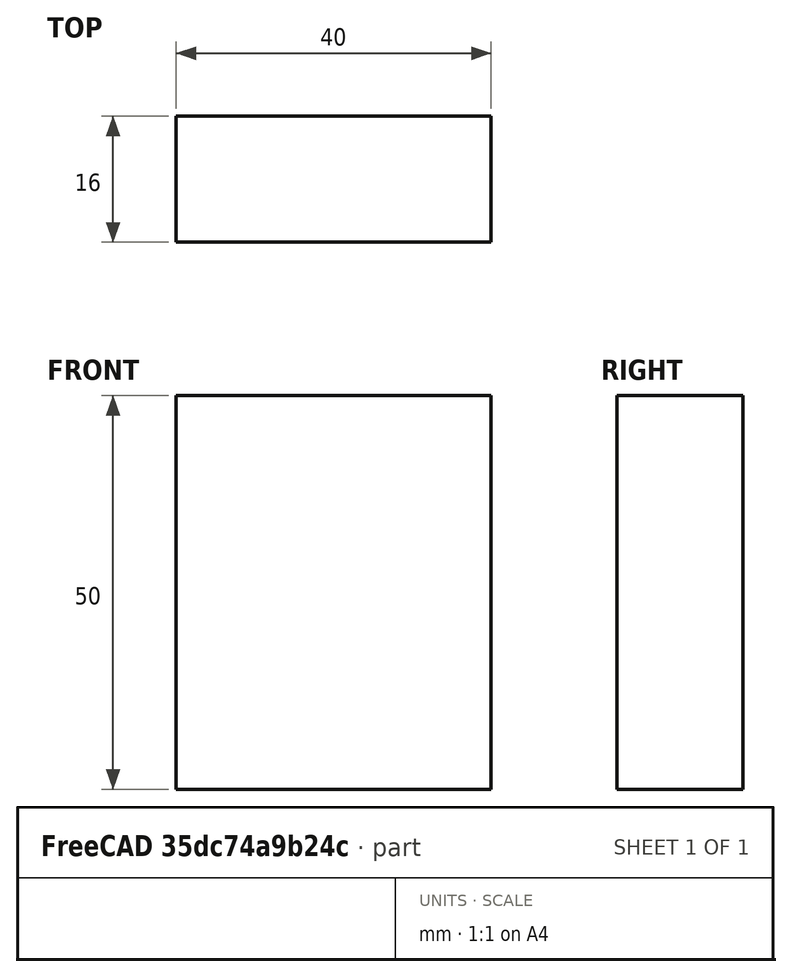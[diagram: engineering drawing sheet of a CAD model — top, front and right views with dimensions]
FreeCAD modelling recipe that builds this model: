
FCSTD DOCUMENT  (FreeCAD 0.15R4671 (Git))
Label: Flat Bar 40x16 EN10058 S235JR
License: All rights reserved
LicenseURL: http://en.wikipedia.org/wiki/All_rights_reserved
objects: Sketcher::SketchObject×1, Part::Extrusion×1
note: 2 computed .brp shape members not serialized (recipe doc carries the construction recipe); baked Part::Feature solids carry a one-line shape summary decoded from their .brp

FEATURE [Sketcher::SketchObject] Sketch
  sketch-geometry (4):
    g0: LineSegment StartX=-20 StartY=-8 StartZ=0 EndX=20 EndY=-8 EndZ=0
    g1: LineSegment StartX=20 StartY=-8 StartZ=0 EndX=20 EndY=8 EndZ=0
    g2: LineSegment StartX=20 StartY=8 StartZ=0 EndX=-20 EndY=8 EndZ=0
    g3: LineSegment StartX=-20 StartY=8 StartZ=0 EndX=-20 EndY=-8 EndZ=0
  constraints (12):
    c: Coincident(g0,g1)
    c: Coincident(g1,g2)
    c: Coincident(g2,g3)
    c: Coincident(g3,g0)
    c: Horizontal(g0)
    c: Horizontal(g2)
    c: Vertical(g1)
    c: Vertical(g3)
    c: Symmetric(g1,g2,g-2)
    c: Symmetric(g0,g1,g-1)
    c: DistanceY(g1) = 16
    c: DistanceX(g0) = 40
FEATURE [Part::Extrusion] Extrude  label="Flat Bar 40x16 EN10058 S235JR"
  Base = -> Sketch
  Dir = (0,0,50)
  Solid = true
